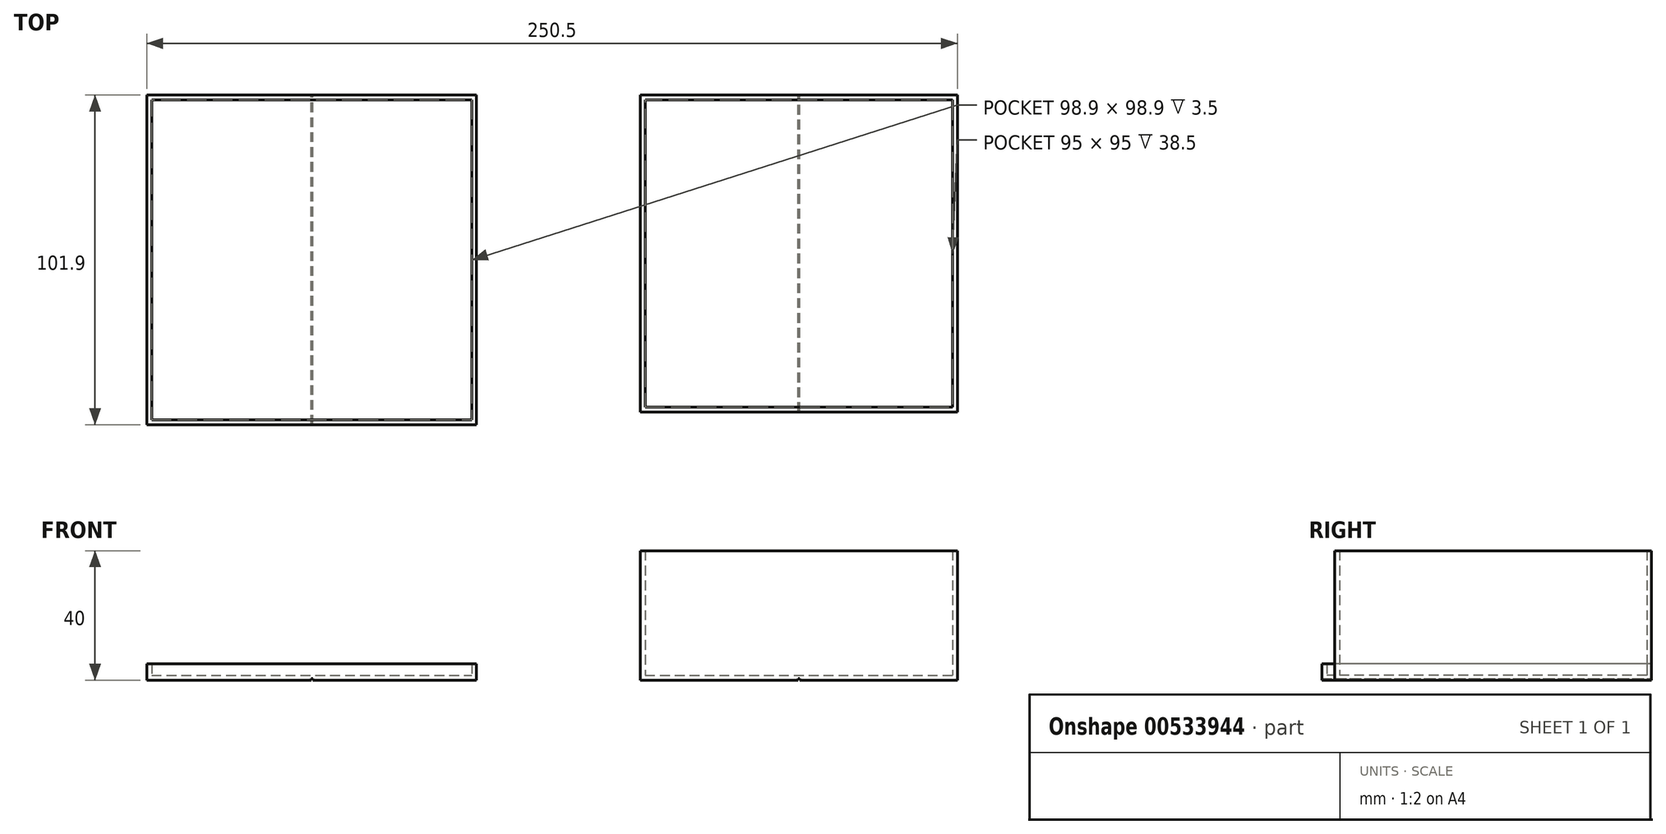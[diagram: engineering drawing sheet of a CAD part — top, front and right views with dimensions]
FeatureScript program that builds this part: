
annotation { "Feature Type Name" : "Feature", "Feature Type Description" : "" }
export const myFeature = defineFeature(function(context is Context, id is Id, definition is map)
    precondition{}
    {
        {
            var Q0;
            Q0=qCreatedBy(makeId("Top.planeOp"),FACE);
            var sketch = newSketch(context, id + "F0", { "sketchPlane" : qUnion([Q0])});
            skLineSegment(sketch, "E0.bottom", {"start": v(-47.5, 47.5) * mm, "end": v(47.5, 47.5) * mm});
            skLineSegment(sketch, "E0.top", {"start": v(-47.5, -47.5) * mm, "end": v(47.5, -47.5) * mm});
            skLineSegment(sketch, "E0.left", {"start": v(-47.5, 47.5) * mm, "end": v(-47.5, -47.5) * mm});
            skLineSegment(sketch, "E0.right", {"start": v(47.5, 47.5) * mm, "end": v(47.5, -47.5) * mm});
            skLineSegment(sketch, "E1.bottom", {"start": v(-49, 49) * mm, "end": v(49, 49) * mm});
            skLineSegment(sketch, "E1.top", {"start": v(-49, -49) * mm, "end": v(49, -49) * mm});
            skLineSegment(sketch, "E1.left", {"start": v(-49, 49) * mm, "end": v(-49, -49) * mm});
            skLineSegment(sketch, "E1.right", {"start": v(49, 49) * mm, "end": v(49, -49) * mm});
            skSolve(sketch);
        }
        {
            var Q0;
            Q0=qCreatedBy(makeId("Top.planeOp"),FACE);
            var sketch = newSketch(context, id + "F1", { "sketchPlane" : qUnion([Q0])});
            skLineSegment(sketch, "E2.bottom", {"start": v(-200, 47.5) * mm, "end": v(-101.1, 47.5) * mm});
            skLineSegment(sketch, "E2.top", {"start": v(-200, -51.4) * mm, "end": v(-101.1, -51.4) * mm});
            skLineSegment(sketch, "E2.left", {"start": v(-200, 47.5) * mm, "end": v(-200, -51.4) * mm});
            skLineSegment(sketch, "E2.right", {"start": v(-101.1, 47.5) * mm, "end": v(-101.1, -51.4) * mm});
            skLineSegment(sketch, "E3.bottom", {"start": v(-201.5, 49) * mm, "end": v(-99.6, 49) * mm});
            skLineSegment(sketch, "E3.top", {"start": v(-201.5, -52.9) * mm, "end": v(-99.6, -52.9) * mm});
            skLineSegment(sketch, "E3.left", {"start": v(-201.5, 49) * mm, "end": v(-201.5, -52.9) * mm});
            skLineSegment(sketch, "E3.right", {"start": v(-99.6, 49) * mm, "end": v(-99.6, -52.9) * mm});
            skLineSegment(sketch, "E4", {"start": v(-150.75, -52.9) * mm, "end": v(-150.75, 49) * mm});
            skLineSegment(sketch, "E5", {"start": v(-150.25, -52.9) * mm, "end": v(-150.25, 49) * mm});
            skSolve(sketch);
        }
        {
            var Q0;
            Q0=makeQuery(id+"F0.imprint","IMPRINT",FACE,{"disambiguationData":[TD([[makeQuery(id+"F0.imprint","IMPRINT",EDGE,{"derivedFrom":sQuery(id+"F0.wireOp",EDGE,"E0.bottom")}),1.0]])]});
            extrude(context, id + "F2", {"entities" : qUnion([Q0]), "depth" : 40 * mm, "offsetDistance" : 25 * mm});
        }
        {
            var Q0;
            Q0=makeQuery(id+"F0.imprint","IMPRINT",FACE,{"disambiguationData":[TD([[makeQuery(id+"F0.imprint","IMPRINT",EDGE,{"derivedFrom":sQuery(id+"F0.wireOp",EDGE,"E0.bottom")}),-1.0]])]});
            extrude(context, id + "F3", {"entities" : qUnion([Q0]), "operationType" : NewBodyOperationType.ADD, "depth" : 1.5 * mm, "offsetDistance" : 25 * mm});
        }
        {
            var Q0;
            Q0=makeQuery(id+"F1.imprint","IMPRINT",FACE,{"disambiguationData":[TD([[makeQuery(id+"F1.imprint","IMPRINT",EDGE,{"derivedFrom":sQuery(id+"F1.wireOp",EDGE,"E2.bottom")}),-1.0]])]});
            extrude(context, id + "F4", {"entities" : qUnion([Q0]), "depth" : 1.5 * mm, "offsetDistance" : 25 * mm});
        }
        {
            var Q0;
            Q0=makeQuery(id+"F1.imprint","IMPRINT",FACE,{"disambiguationData":[TD([[makeQuery(id+"F1.imprint","IMPRINT",EDGE,{"derivedFrom":sQuery(id+"F1.wireOp",EDGE,"E2.bottom")}),1.0]])]});
            var Q1;
            {var subQ0=sQuery(id+"F1.wireOp",EDGE,"E2.left");Q1=makeQuery(id+"F1.imprint","IMPRINT",FACE,{"disambiguationData":[TD([[makeQuery(id+"F1.imprint","IMPRINT",EDGE,{"derivedFrom":subQ0}),-1.0]])]});}
            var Q2;
            {var subQ6=sQuery(id+"F1.wireOp",EDGE,"E2.right");Q2=makeQuery(id+"F1.imprint","IMPRINT",FACE,{"disambiguationData":[TD([[makeQuery(id+"F1.imprint","IMPRINT",EDGE,{"derivedFrom":subQ6}),1.0]])]});}
            var Q3;
            {var subQ0=sQuery(id+"F1.wireOp",EDGE,"E4");var subQ1=sQuery(id+"F1.wireOp",EDGE,"E2.top");var subQ2=makeQuery(id+"F1.imprint","INTERSECT",VERTEX,{"derivedFrom":[subQ1,subQ0]});Q3=makeQuery(id+"F1.imprint","IMPRINT",FACE,{"disambiguationData":[TD([[makeQuery(id+"F1.imprint","IMPRINT",EDGE,{"disambiguationData":[TD([[subQ2,-1.0]])],"derivedFrom":subQ1}),-1.0]])]});}
            extrude(context, id + "F5", {"entities" : qUnion([Q0, Q1, Q2, Q3]), "operationType" : NewBodyOperationType.ADD, "depth" : 5 * mm, "offsetDistance" : 25 * mm});
        }
        {
            var Q0;
            {var subQ0=sQuery(id+"F0.wireOp",EDGE,"E0.right");var subQ1=sQuery(id+"F0.wireOp",EDGE,"E0.left");var subQ2=sQuery(id+"F0.wireOp",EDGE,"E0.top");var subQ3=sQuery(id+"F0.wireOp",EDGE,"E0.bottom");Q0=makeQuery(id+"F3.boolean.opBoolean","MERGE",FACE,{"derivedFrom":[makeQuery(id+"F2.opExtrude","CAP_FACE",FACE,{"disambiguationData":[OSD([subQ3,subQ2,subQ1,subQ0,sQuery(id+"F0.wireOp",EDGE,"E1.bottom"),sQuery(id+"F0.wireOp",EDGE,"E1.top"),sQuery(id+"F0.wireOp",EDGE,"E1.left"),sQuery(id+"F0.wireOp",EDGE,"E1.right")])],"isStart":true}),makeQuery(id+"F3.opExtrude","CAP_FACE",FACE,{"disambiguationData":[OSD([subQ3,subQ2,subQ1,subQ0])],"isStart":true})]});}
            var sketch = newSketch(context, id + "F6", { "sketchPlane" : qUnion([Q0])});
            skLineSegment(sketch, "E6", {"start": v(-0.25, 49) * mm, "end": v(-0.25, -49) * mm});
            skLineSegment(sketch, "E7", {"start": v(0.25, 49) * mm, "end": v(0.25, -49) * mm});
            skSolve(sketch);
        }
        {
            var Q0;
            {var subQ0=sQuery(id+"F6.wireOp",EDGE,"E6");Q0=makeQuery(id+"F6.imprint","IMPRINT",FACE,{"disambiguationData":[TD([[makeQuery(id+"F6.imprint","IMPRINT",EDGE,{"derivedFrom":subQ0}),1.0]])]});}
            extrude(context, id + "F7", {"entities" : qUnion([Q0]), "operationType" : NewBodyOperationType.REMOVE, "oppositeDirection" : true, "depth" : 0.5 * mm, "offsetDistance" : 25 * mm});
        }
        {
            var Q0;
            {var subQ0=sQuery(id+"F1.wireOp",EDGE,"E4");var subQ1=sQuery(id+"F1.wireOp",EDGE,"E2.bottom");var subQ2=makeQuery(id+"F1.imprint","INTERSECT",VERTEX,{"derivedFrom":[subQ1,subQ0]});Q0=makeQuery(id+"F1.imprint","IMPRINT",FACE,{"disambiguationData":[TD([[makeQuery(id+"F1.imprint","IMPRINT",EDGE,{"disambiguationData":[TD([[subQ2,-1.0]])],"derivedFrom":subQ1}),-1.0]])]});}
            var Q1;
            {var subQ0=sQuery(id+"F1.wireOp",EDGE,"E4");var subQ1=sQuery(id+"F1.wireOp",EDGE,"E2.top");var subQ2=makeQuery(id+"F1.imprint","INTERSECT",VERTEX,{"derivedFrom":[subQ1,subQ0]});Q1=makeQuery(id+"F1.imprint","IMPRINT",FACE,{"disambiguationData":[TD([[makeQuery(id+"F1.imprint","IMPRINT",EDGE,{"disambiguationData":[TD([[subQ2,-1.0]])],"derivedFrom":subQ1}),-1.0]])]});}
            var Q2;
            {var subQ0=sQuery(id+"F1.wireOp",EDGE,"E4");var subQ1=sQuery(id+"F1.wireOp",EDGE,"E2.bottom");var subQ2=makeQuery(id+"F1.imprint","INTERSECT",VERTEX,{"derivedFrom":[subQ1,subQ0]});Q2=makeQuery(id+"F1.imprint","IMPRINT",FACE,{"disambiguationData":[TD([[makeQuery(id+"F1.imprint","IMPRINT",EDGE,{"disambiguationData":[TD([[subQ2,-1.0]])],"derivedFrom":subQ1}),1.0]])]});}
            extrude(context, id + "F8", {"entities" : qUnion([Q0, Q1, Q2]), "operationType" : NewBodyOperationType.REMOVE, "oppositeDirection" : true, "depth" : -0.5 * mm, "offsetDistance" : 25 * mm});
        }
    });
